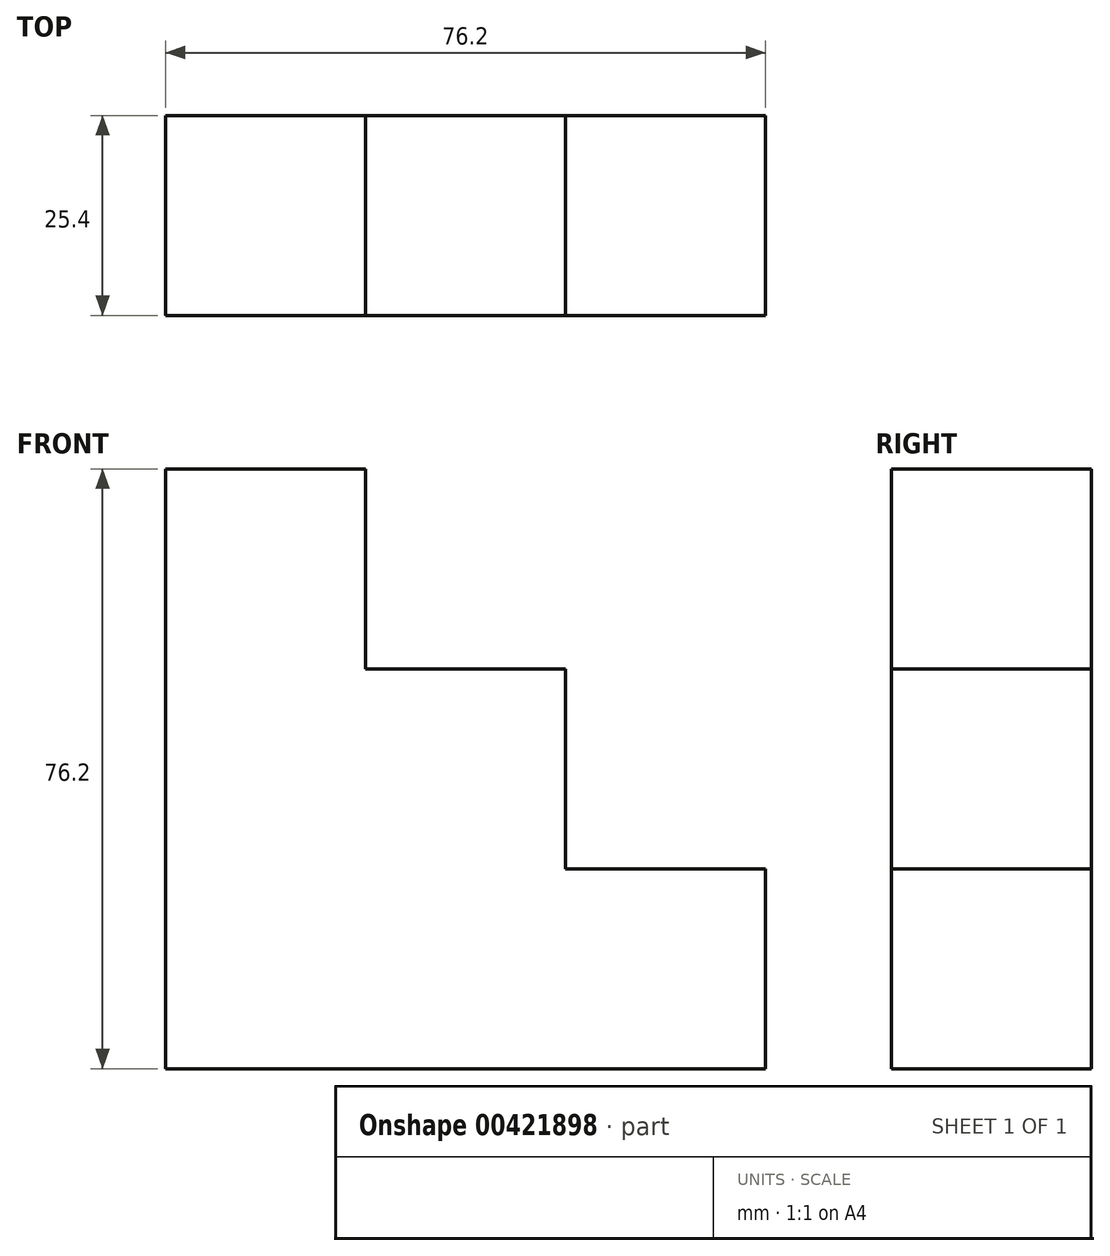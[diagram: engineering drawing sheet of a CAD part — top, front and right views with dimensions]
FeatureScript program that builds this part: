
annotation { "Feature Type Name" : "Feature", "Feature Type Description" : "" }
export const myFeature = defineFeature(function(context is Context, id is Id, definition is map)
    precondition{}
    {
        {
            var Q0;
            Q0=qCreatedBy(makeId("Front.planeOp"),FACE);
            var sketch = newSketch(context, id + "F0", { "sketchPlane" : qUnion([Q0])});
            skLineSegment(sketch, "E0", {"start": v(33.73, 0) * mm, "end": v(-42.47, 0) * mm});
            skLineSegment(sketch, "E1", {"start": v(-42.47, 0) * mm, "end": v(-42.47, 76.2) * mm});
            skLineSegment(sketch, "E2", {"start": v(-42.47, 76.2) * mm, "end": v(-17.07, 76.2) * mm});
            skLineSegment(sketch, "E3", {"start": v(-17.07, 76.2) * mm, "end": v(-17.07, 50.8) * mm});
            skLineSegment(sketch, "E4", {"start": v(-17.07, 50.8) * mm, "end": v(8.33, 50.8) * mm});
            skLineSegment(sketch, "E5", {"start": v(8.33, 50.8) * mm, "end": v(8.33, 25.4) * mm});
            skLineSegment(sketch, "E6", {"start": v(8.33, 25.4) * mm, "end": v(33.73, 25.4) * mm});
            skLineSegment(sketch, "E7", {"start": v(33.73, 25.4) * mm, "end": v(33.73, 0) * mm});
            skSolve(sketch);
        }
        {
            var Q0;
            Q0=makeQuery(id+"F0.imprint","IMPRINT",FACE,{"disambiguationData":[TD([[makeQuery(id+"F0.imprint","IMPRINT",EDGE,{"derivedFrom":sQuery(id+"F0.wireOp",EDGE,"E0")}),-1.0]])]});
            extrude(context, id + "F1", {"entities" : qUnion([Q0]), "depth" : 25.4 * mm});
        }
    });
